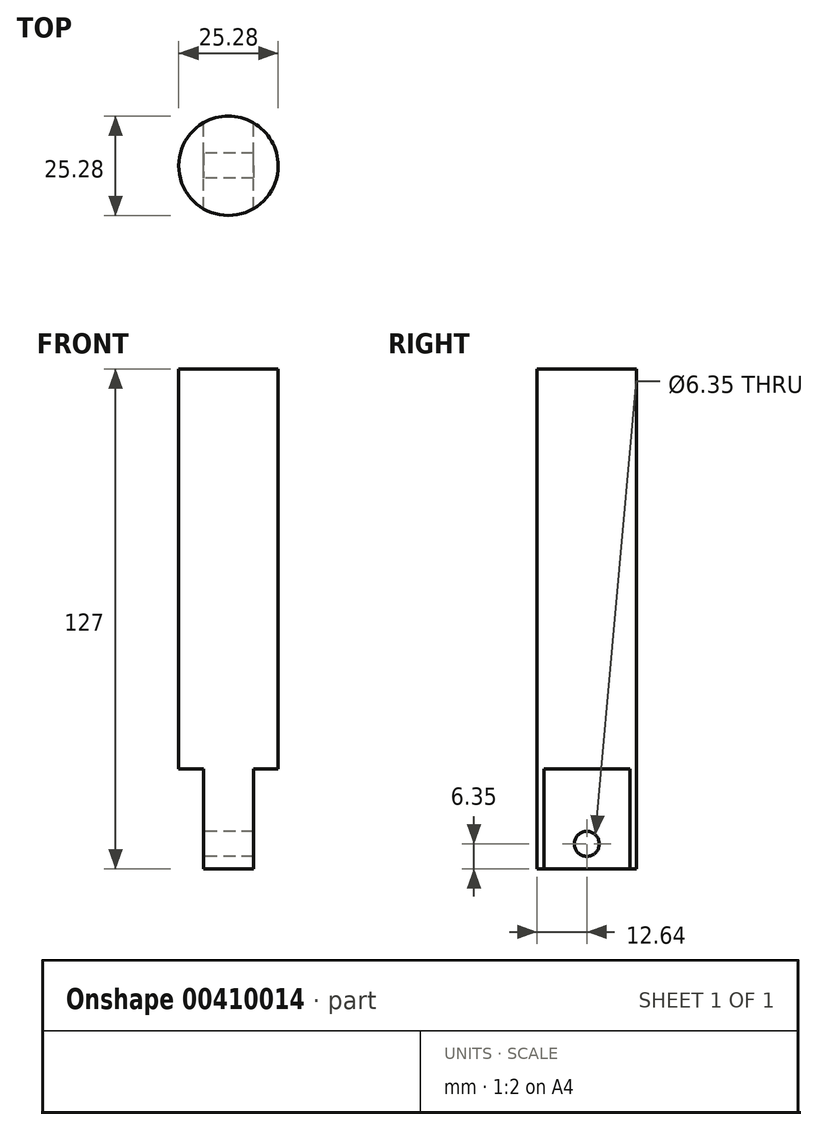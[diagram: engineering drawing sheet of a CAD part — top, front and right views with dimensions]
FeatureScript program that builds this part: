
annotation { "Feature Type Name" : "Feature", "Feature Type Description" : "" }
export const myFeature = defineFeature(function(context is Context, id is Id, definition is map)
    precondition{}
    {
        {
            var Q0;
            Q0=qCreatedBy(makeId("Top.planeOp"),FACE);
            var sketch = newSketch(context, id + "F0", { "sketchPlane" : qUnion([Q0])});
            skCircle(sketch, "E0", {"center": v(0, 0) * mm, "radius": 12.64 * mm});
            skSolve(sketch);
        }
        {
            var Q0;
            Q0=makeQuery(id+"F0.imprint","IMPRINT",FACE,{"disambiguationData":[TD([[makeQuery(id+"F0.imprint","IMPRINT",EDGE,{"derivedFrom":sQuery(id+"F0.wireOp",EDGE,"E0")}),1.0]])]});
            extrude(context, id + "F1", {"entities" : qUnion([Q0]), "depth" : 127 * mm});
        }
        {
            var Q0;
            Q0=qCreatedBy(makeId("Front.planeOp"),FACE);
            var sketch = newSketch(context, id + "F2", { "sketchPlane" : qUnion([Q0])});
            skLineSegment(sketch, "E1.bottom", {"start": v(-19.87, -10.64) * mm, "end": v(-6.35, -10.64) * mm});
            skLineSegment(sketch, "E1.top", {"start": v(-19.87, 25.4) * mm, "end": v(-6.35, 25.4) * mm});
            skLineSegment(sketch, "E1.left", {"start": v(-19.87, -10.64) * mm, "end": v(-19.87, 25.4) * mm});
            skLineSegment(sketch, "E1.right", {"start": v(-6.35, -10.64) * mm, "end": v(-6.35, 25.4) * mm});
            skLineSegment(sketch, "E2.MirrorCS", {"start": v(6.35, -10.64) * mm, "end": v(6.35, 25.4) * mm});
            skLineSegment(sketch, "E3.MirrorCS", {"start": v(19.87, 25.4) * mm, "end": v(6.35, 25.4) * mm});
            skLineSegment(sketch, "E4.MirrorCS", {"start": v(19.87, -10.64) * mm, "end": v(19.87, 25.4) * mm});
            skLineSegment(sketch, "E5.MirrorCS", {"start": v(19.87, -10.64) * mm, "end": v(6.35, -10.64) * mm});
            skSolve(sketch);
        }
        {
            var Q0;
            Q0=makeQuery(id+"F2.imprint","IMPRINT",FACE,{"disambiguationData":[TD([[makeQuery(id+"F2.imprint","IMPRINT",EDGE,{"derivedFrom":sQuery(id+"F2.wireOp",EDGE,"E1.bottom")}),1.0]])]});
            var Q1;
            Q1=makeQuery(id+"F2.imprint","IMPRINT",FACE,{"disambiguationData":[TD([[makeQuery(id+"F2.imprint","IMPRINT",EDGE,{"derivedFrom":sQuery(id+"F2.wireOp",EDGE,"E2.MirrorCS")}),-1.0]])]});
            extrude(context, id + "F3", {"entities" : qUnion([Q0, Q1]), "operationType" : NewBodyOperationType.REMOVE, "endBound" : BoundingType.SYMMETRIC, "oppositeDirection" : true, "depth" : 25.4 * mm});
        }
        {
            var Q0;
            Q0=makeQuery(id+"F3.boolean.opBoolean","COPY",FACE,{"derivedFrom":makeQuery(id+"F3.opExtrude","SWEPT_FACE",FACE,{"disambiguationData":[OSD([sQuery(id+"F2.wireOp",EDGE,"E1.right")])]})});
            var sketch = newSketch(context, id + "F4", { "sketchPlane" : qUnion([Q0])});
            skCircle(sketch, "E6", {"center": v(0, 6.35) * mm, "radius": 3.18 * mm});
            skSolve(sketch);
        }
        {
            var Q0;
            Q0=makeQuery(id+"F4.imprint","IMPRINT",FACE,{"disambiguationData":[TD([[makeQuery(id+"F4.imprint","IMPRINT",EDGE,{"derivedFrom":sQuery(id+"F4.wireOp",EDGE,"E6")}),1.0]])]});
            extrude(context, id + "F5", {"entities" : qUnion([Q0]), "operationType" : NewBodyOperationType.REMOVE, "oppositeDirection" : true, "depth" : 25.4 * mm});
        }
    });
